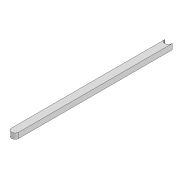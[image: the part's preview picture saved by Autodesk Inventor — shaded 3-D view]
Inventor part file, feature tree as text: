
AUTODESK INVENTOR PART (.ipt)
format: ipt  version: 2022 (Build 260153000, 153)  size: 77,824 bytes
history: native  units: mm
features: extrude x1, sketch x1
ambient origin geometry x8: Origin, YZ Plane, XZ Plane, XY Plane, X Axis, Y Axis, Z Axis, Center Point
bodies: Solid1 (feature_tree)
feature tree (2):
  extrude  "Extrusion1"  Depth=8.0mm
  sketch  "Sketch1"  dims[d0=170.0mm d1=8.0mm d2=6.0mm d3=0.0mm]
